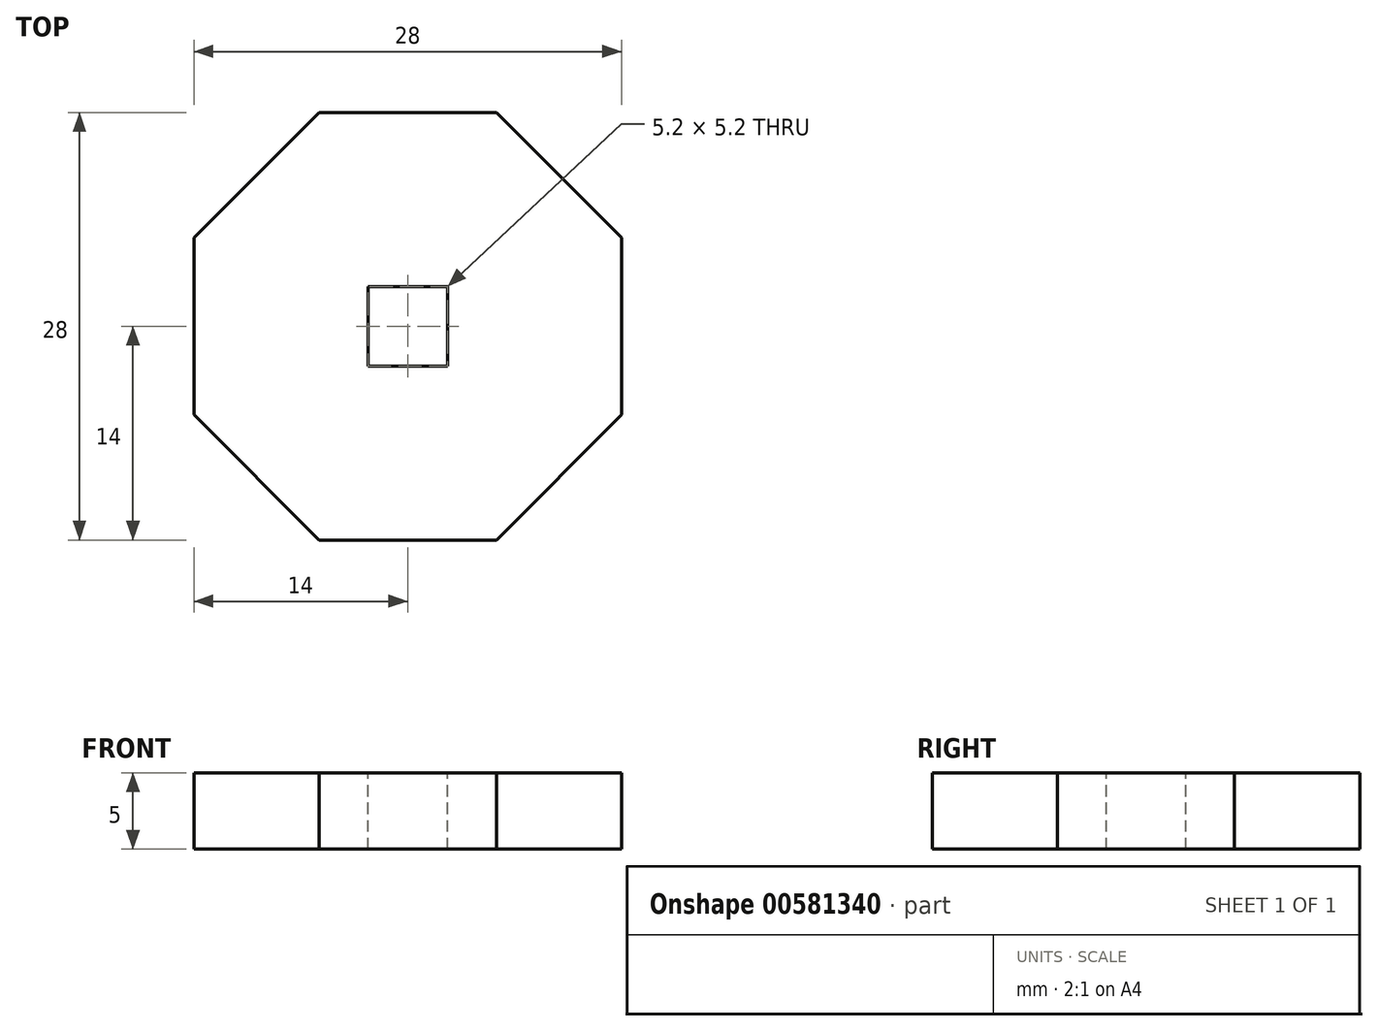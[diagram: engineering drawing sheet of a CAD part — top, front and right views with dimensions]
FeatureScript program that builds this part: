
annotation { "Feature Type Name" : "Feature", "Feature Type Description" : "" }
export const myFeature = defineFeature(function(context is Context, id is Id, definition is map)
    precondition{}
    {
        {
            var Q0;
            Q0=qCreatedBy(makeId("Top.planeOp"),FACE);
            var sketch = newSketch(context, id + "F0", { "sketchPlane" : qUnion([Q0])});
            skCircle(sketch, "E0.cCircle", {"center": v(0, 0) * mm, "radius": 14 * mm, "construction": true});
            skLineSegment(sketch, "E0.0", {"start": v(5.8, -14) * mm, "end": v(-5.8, -14) * mm});
            skLineSegment(sketch, "E0.1", {"start": v(-5.8, -14) * mm, "end": v(-14, -5.8) * mm});
            skLineSegment(sketch, "E0.2", {"start": v(-14, -5.8) * mm, "end": v(-14, 5.8) * mm});
            skLineSegment(sketch, "E0.3", {"start": v(-14, 5.8) * mm, "end": v(-5.8, 14) * mm});
            skLineSegment(sketch, "E0.4", {"start": v(-5.8, 14) * mm, "end": v(5.8, 14) * mm});
            skLineSegment(sketch, "E0.5", {"start": v(5.8, 14) * mm, "end": v(14, 5.8) * mm});
            skLineSegment(sketch, "E0.6", {"start": v(14, 5.8) * mm, "end": v(14, -5.8) * mm});
            skLineSegment(sketch, "E0.7", {"start": v(14, -5.8) * mm, "end": v(5.8, -14) * mm});
            skPoint(sketch, "E0.0.midPoint", {"position": v(0, -14) * mm});
            skSolve(sketch);
        }
        {
            var Q0;
            Q0 = qSketchRegion(id + "F0", true);
            extrude(context, id + "F1", {"entities" : qUnion([Q0]), "depth" : 5 * mm, "offsetDistance" : 25 * mm});
        }
        {
            var Q0;
            Q0=makeQuery(id+"F1.opExtrude","CAP_FACE",FACE,{"disambiguationData":[OSD([sQuery(id+"F0.wireOp",EDGE,"E0.0"),sQuery(id+"F0.wireOp",EDGE,"E0.1"),sQuery(id+"F0.wireOp",EDGE,"E0.2"),sQuery(id+"F0.wireOp",EDGE,"E0.3"),sQuery(id+"F0.wireOp",EDGE,"E0.4"),sQuery(id+"F0.wireOp",EDGE,"E0.5"),sQuery(id+"F0.wireOp",EDGE,"E0.6"),sQuery(id+"F0.wireOp",EDGE,"E0.7")])],"isStart":false});
            var sketch = newSketch(context, id + "F2", { "sketchPlane" : qUnion([Q0])});
            skLineSegment(sketch, "E1.bottom", {"start": v(2.6, -2.6) * mm, "end": v(-2.6, -2.6) * mm});
            skLineSegment(sketch, "E1.top", {"start": v(2.6, 2.6) * mm, "end": v(-2.6, 2.6) * mm});
            skLineSegment(sketch, "E1.left", {"start": v(2.6, -2.6) * mm, "end": v(2.6, 2.6) * mm});
            skLineSegment(sketch, "E1.right", {"start": v(-2.6, -2.6) * mm, "end": v(-2.6, 2.6) * mm});
            skPoint(sketch, "E1.middle", {"position": v(0, 0) * mm});
            skSolve(sketch);
        }
        {
            var Q0;
            Q0=makeQuery(id+"F2.imprint","IMPRINT",FACE,{"disambiguationData":[TD([[makeQuery(id+"F2.imprint","IMPRINT",EDGE,{"derivedFrom":sQuery(id+"F2.wireOp",EDGE,"E1.bottom")}),-1.0]])]});
            extrude(context, id + "F3", {"entities" : qUnion([Q0]), "operationType" : NewBodyOperationType.REMOVE, "oppositeDirection" : true, "depth" : 25 * mm, "offsetDistance" : 25 * mm});
        }
    });
